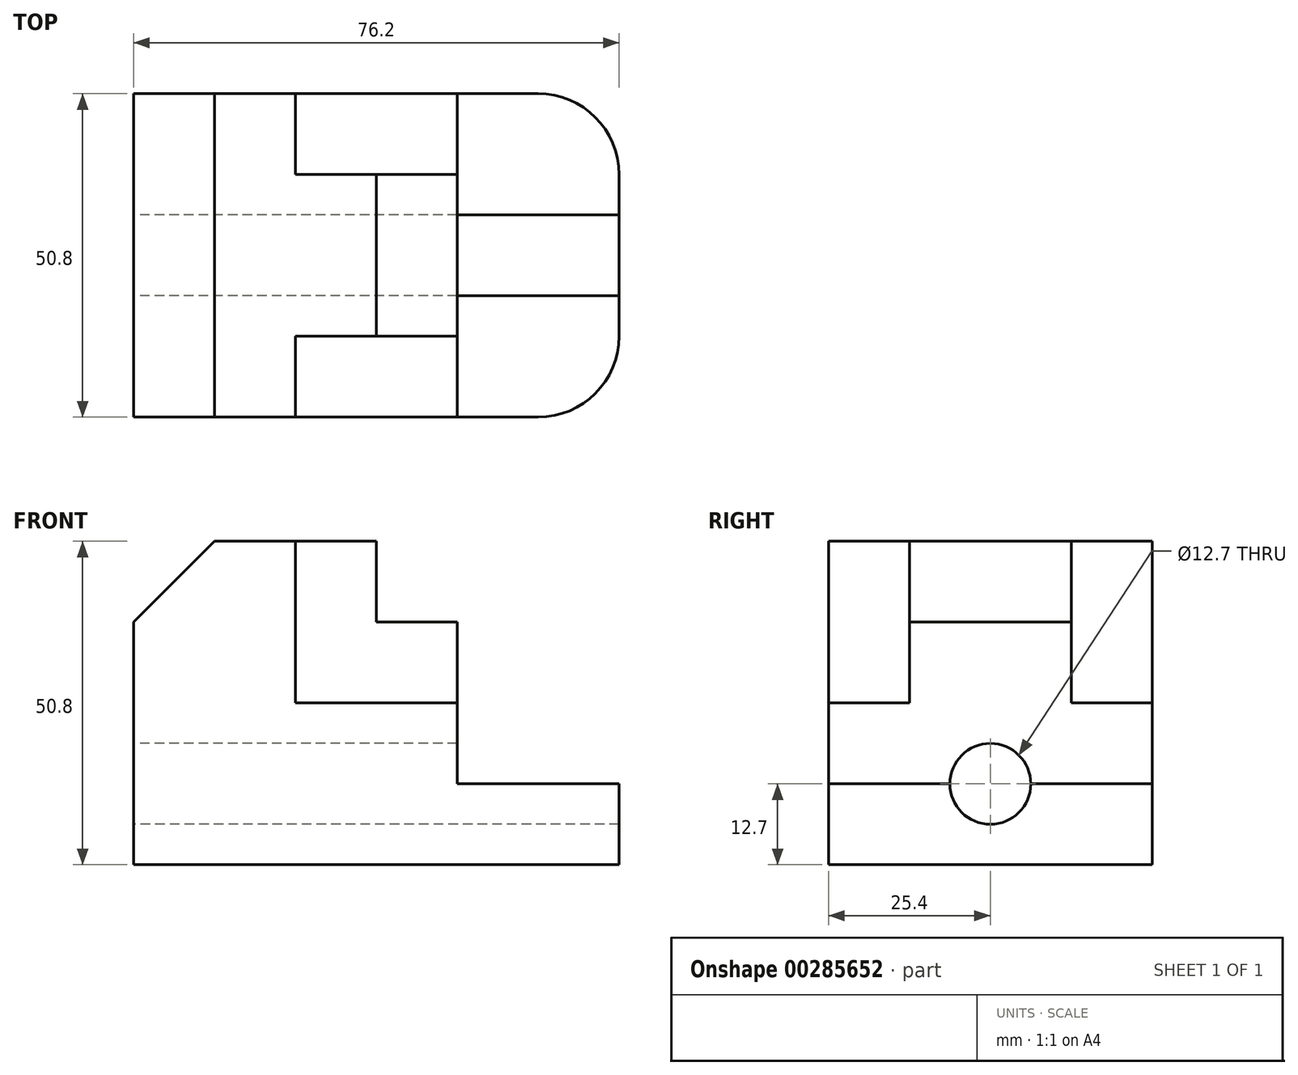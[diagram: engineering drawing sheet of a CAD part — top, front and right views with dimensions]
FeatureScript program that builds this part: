
annotation { "Feature Type Name" : "Feature", "Feature Type Description" : "" }
export const myFeature = defineFeature(function(context is Context, id is Id, definition is map)
    precondition{}
    {
        {
            var Q0;
            Q0=qCreatedBy(makeId("Front.planeOp"),FACE);
            var sketch = newSketch(context, id + "F0", { "sketchPlane" : qUnion([Q0])});
            skLineSegment(sketch, "E0", {"start": v(0, 0) * mm, "end": v(0, 38.1) * mm});
            skLineSegment(sketch, "E1", {"start": v(0, 38.1) * mm, "end": v(12.7, 50.8) * mm});
            skLineSegment(sketch, "E2", {"start": v(12.7, 50.8) * mm, "end": v(25.4, 50.8) * mm});
            skLineSegment(sketch, "E3", {"start": v(25.4, 50.8) * mm, "end": v(25.4, 25.4) * mm});
            skLineSegment(sketch, "E4", {"start": v(25.4, 25.4) * mm, "end": v(50.8, 25.4) * mm});
            skLineSegment(sketch, "E5", {"start": v(50.8, 25.4) * mm, "end": v(50.8, 12.7) * mm});
            skLineSegment(sketch, "E6", {"start": v(50.8, 12.7) * mm, "end": v(76.2, 12.7) * mm});
            skLineSegment(sketch, "E7", {"start": v(76.2, 12.7) * mm, "end": v(76.2, 0) * mm});
            skLineSegment(sketch, "E8", {"start": v(76.2, 0) * mm, "end": v(0, 0) * mm});
            skSolve(sketch);
        }
        {
            var Q0;
            Q0 = qSketchRegion(id + "F0", true);
            extrude(context, id + "F1", {"entities" : qUnion([Q0]), "endBound" : BoundingType.SYMMETRIC, "depth" : 50.8 * mm});
        }
        {
            var Q0;
            Q0=qCreatedBy(makeId("Front.planeOp"),FACE);
            var sketch = newSketch(context, id + "F2", { "sketchPlane" : qUnion([Q0])});
            skLineSegment(sketch, "E9", {"start": v(25.4, 50.8) * mm, "end": v(25.4, 25.4) * mm});
            skLineSegment(sketch, "E10", {"start": v(25.4, 25.4) * mm, "end": v(50.8, 25.4) * mm});
            skLineSegment(sketch, "E11", {"start": v(50.8, 25.4) * mm, "end": v(50.8, 38.1) * mm});
            skLineSegment(sketch, "E12", {"start": v(50.8, 38.1) * mm, "end": v(38.1, 38.1) * mm});
            skLineSegment(sketch, "E13", {"start": v(38.1, 38.1) * mm, "end": v(38.1, 50.8) * mm});
            skLineSegment(sketch, "E14", {"start": v(38.1, 50.8) * mm, "end": v(25.4, 50.8) * mm});
            skSolve(sketch);
        }
        {
            var Q0;
            Q0 = qSketchRegion(id + "F2", true);
            extrude(context, id + "F3", {"entities" : qUnion([Q0]), "operationType" : NewBodyOperationType.ADD, "endBound" : BoundingType.SYMMETRIC, "depth" : 25.4 * mm});
        }
        {
            var Q0;
            Q0=qCreatedBy(makeId("Right.planeOp"),FACE);
            var sketch = newSketch(context, id + "F4", { "sketchPlane" : qUnion([Q0])});
            skCircle(sketch, "E15", {"center": v(0, 12.7) * mm, "radius": 6.35 * mm});
            skSolve(sketch);
        }
        {
            var Q0;
            Q0 = qSketchRegion(id + "F4", true);
            extrude(context, id + "F5", {"entities" : qUnion([Q0]), "operationType" : NewBodyOperationType.REMOVE, "depth" : 76.2 * mm});
        }
        {
            var Q0;
            Q0=qCreatedBy(makeId("Top.planeOp"),FACE);
            var sketch = newSketch(context, id + "F6", { "sketchPlane" : qUnion([Q0])});
            skLineSegment(sketch, "E16", {"start": v(63.5, 36.1) * mm, "end": v(63.5, -28.28) * mm, "construction": true});
            skLineSegment(sketch, "E17", {"start": v(42.63, 12.7) * mm, "end": v(79.67, 12.7) * mm, "construction": true});
            skLineSegment(sketch, "E18", {"start": v(46.1, -12.7) * mm, "end": v(84.58, -12.7) * mm, "construction": true});
            skArc(sketch, "E19", {"start": v(76.2, 12.7) * mm, "mid": v(72.48, 21.68) * mm, "end": v(63.5, 25.4) * mm});
            skArc(sketch, "E20", {"start": v(63.5, -25.4) * mm, "mid": v(72.48, -21.68) * mm, "end": v(76.2, -12.7) * mm});
            skLineSegment(sketch, "E21", {"start": v(63.5, 25.4) * mm, "end": v(76.2, 25.4) * mm});
            skLineSegment(sketch, "E22", {"start": v(76.2, 25.4) * mm, "end": v(76.2, 12.7) * mm});
            skLineSegment(sketch, "E23", {"start": v(76.2, -12.7) * mm, "end": v(76.2, -25.4) * mm});
            skLineSegment(sketch, "E24", {"start": v(63.5, -25.4) * mm, "end": v(76.2, -25.4) * mm});
            skSolve(sketch);
        }
        {
            var Q0;
            Q0 = qSketchRegion(id + "F6", true);
            extrude(context, id + "F7", {"entities" : qUnion([Q0]), "operationType" : NewBodyOperationType.REMOVE, "depth" : 25.4 * mm});
        }
    });
